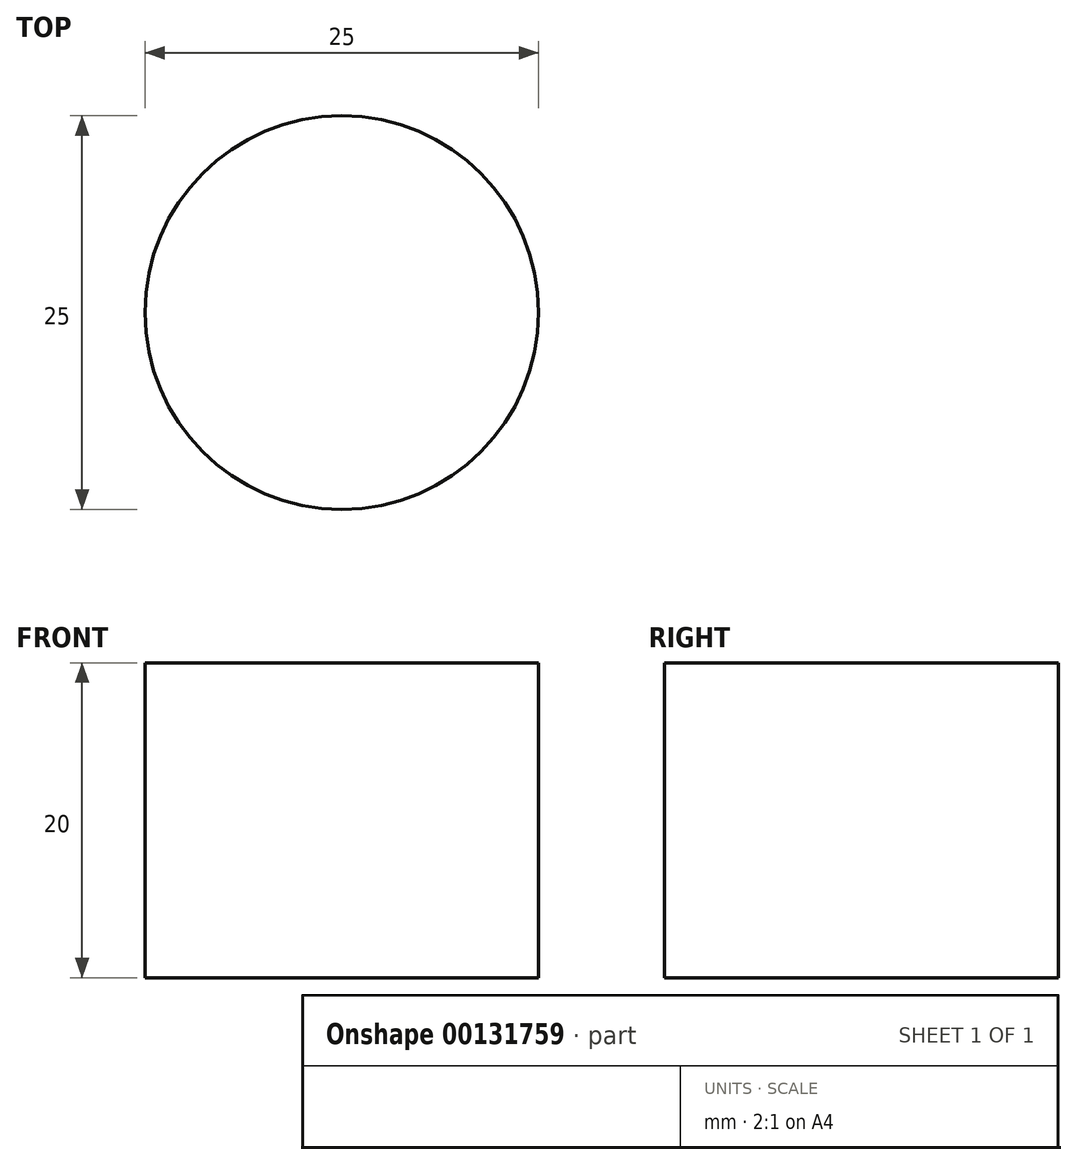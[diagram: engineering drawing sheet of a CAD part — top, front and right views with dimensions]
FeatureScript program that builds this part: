
annotation { "Feature Type Name" : "Feature", "Feature Type Description" : "" }
export const myFeature = defineFeature(function(context is Context, id is Id, definition is map)
    precondition{}
    {
        {
            var Q0;
            Q0=qCreatedBy(makeId("Top.planeOp"),FACE);
            var sketch = newSketch(context, id + "F0", { "sketchPlane" : qUnion([Q0])});
            skCircle(sketch, "E0", {"center": v(0, 0) * mm, "radius": 12.5 * mm});
            skLineSegment(sketch, "E1", {"start": v(0, 0) * mm, "end": v(10.83, 6.25) * mm});
            skLineSegment(sketch, "E2", {"start": v(0, 0) * mm, "end": v(-10.83, 6.25) * mm});
            skLineSegment(sketch, "E3", {"start": v(0, 0) * mm, "end": v(0, -12.5) * mm});
            skCircle(sketch, "E4", {"center": v(-6.93, 4) * mm, "radius": 3.25 * mm});
            skCircle(sketch, "E5", {"center": v(6.93, 4) * mm, "radius": 3.25 * mm});
            skCircle(sketch, "E6", {"center": v(0, -8) * mm, "radius": 3.25 * mm});
            skSolve(sketch);
        }
        {
            var Q0;
            Q0=makeQuery(id+"F0.imprint","IMPRINT",FACE,{"disambiguationData":[TD([[makeQuery(id+"F0.imprint","IMPRINT",EDGE,{"derivedFrom":sQuery(id+"F0.wireOp",EDGE,"E0")}),1.0]])]});
            var Q1;
            Q1=makeQuery(id+"F0.imprint","IMPRINT",FACE,{"disambiguationData":[TD([[makeQuery(id+"F0.imprint","IMPRINT",EDGE,{"derivedFrom":sQuery(id+"F0.wireOp",EDGE,"E4")}),1.0]])]});
            var Q2;
            Q2=makeQuery(id+"F0.imprint","IMPRINT",FACE,{"disambiguationData":[TD([[makeQuery(id+"F0.imprint","IMPRINT",EDGE,{"derivedFrom":sQuery(id+"F0.wireOp",EDGE,"E5")}),1.0]])]});
            var Q3;
            Q3=makeQuery(id+"F0.imprint","IMPRINT",FACE,{"disambiguationData":[TD([[makeQuery(id+"F0.imprint","IMPRINT",EDGE,{"derivedFrom":sQuery(id+"F0.wireOp",EDGE,"E6")}),1.0]])]});
            extrude(context, id + "F1", {"entities" : qUnion([Q0, Q1, Q2, Q3]), "depth" : 20 * mm});
        }
    });
